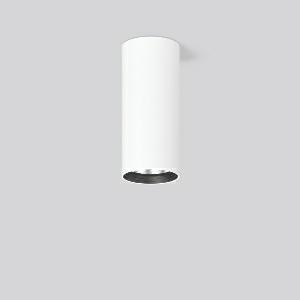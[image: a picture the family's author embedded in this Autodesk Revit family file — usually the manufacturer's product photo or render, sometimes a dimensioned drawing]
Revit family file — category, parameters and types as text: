
# Revit family: heledon_mini_a_931208_002_2_ae0f
name_source: partatom
category: Lighting Fixtures
units: mm (PartAtom-declared; Revit-internal decimal feet)

## family parameters
Cut with Voids When Loaded = No
Host = Face
Light Source = No
Part Type = Normal
Room Calculation Point = No
Round Connector Dimension = Use Diameter
Shared = No

## types (1)
- HELEDON mini A (1 x LED Modul 927, 3400 lm, 2700)
    Apparent Load = 29 VA
    Approval mark = CE
    CIE Flux Codes = 100 100 100 100 100
    Color Rendering = 92
    Color Temperature = 2700
    Default Elevation = 1800 mm
    Description = Series: HELEDON mini
Cylindrical surface-mounted downlight. Housing: die-cast aluminium, powder-coated. Internal ceiling frame polycarbonate with bayonet mounting. Black plastic ring and recessed LED to prevent glare from the side. Optical assembly with reflector made of MIRO-Silver with 98% total light reflection for outstanding efficiency - can be changed without tools. Best colour rendering index Ra>90. Suitable for Ceiling mounting. Easy installation with a separate ceiling frame with bayonet mounting and plug connection. Driver integrated. Connected via plug-in connector. High quality converter without flickering and stroboscopic effect. The following accessories can be mounted without use of tools: interchangeable lenses, decorative glasses, honeycomb louvre, clear and frosted diffusers, white interchangeable plastic ring. 
Colour: traffic white, matt (RAL 9016)
Diameter: 87 mm
Height: 197 mm
Lamp: LED
Socket: without socket
Colour temperature: 2700K
Colour rendering index (CRI): 92
System power: 29 W
Rated luminous flux: 3400 lm
Luminous efficiency: 117 lm/W
Control gear: Regulated power supply
Protection class: I
Type of protection: IP 20
    Height = 197 mm
    Lamp = 1 x LED Modul 927
    Lamp Light Flux = 3400 lm
    Lamp count = 1
    Length = 87 mm
    Lifetime = 50000 h
    Luminous efficacy = 117 lm/W
    Manufacturer = RZB
    ModVariant = No
    Model = 931208.002.2
    Mounting Place = Ceiling
    Mounting Type = Surface mounted
    Number of Poles = 1
    OnlyDefault = Yes
    Power Factor = 1
    Product Name = HELEDON mini A
    Product group = Surface mounted downlights
    ProductGroupID = 302
    Protection Class = Protection class I
    Protection Degree = IP 20
    RLX_Detail_Level = 1
    RLX_Emergency_Light_Flux = 0 lm
    RLX_Emergency_Type = 0
    RLX_Emergency_Type_DB = No
    RlxData = <blob elided: 107597 chars, md5=8ba4558f>
    Socket = socket
    Standby Power = 0 W
    System Light Flux = 3400 lm
    System Power = 29 W
    Type Comments = Product without accessories
    Type Image = 931188.002.jpg
    URL = http://relux.com
    VarID = ---
    Voltage = 230 V
    Voltage Range = 220-240 V
    Weight = 0.00 kg
    Width = 0 mm  [stored 0 ft]

note: [stored X ft] marks values corroborated as IEEE doubles in the binary element streams (Revit-internal decimal feet)

## geometry (parser evidence)
native form markers: Blend x4, Sweep x8
no freeform markers — native parametric forms only
